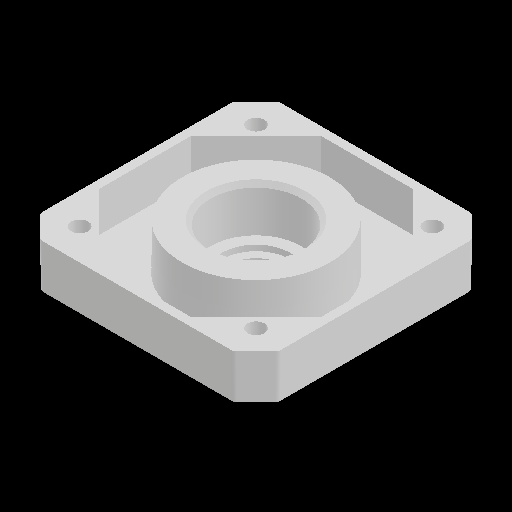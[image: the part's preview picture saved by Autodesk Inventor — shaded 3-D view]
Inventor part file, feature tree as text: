
AUTODESK INVENTOR PART (.ipt)
format: ipt  version: 2023 (Build 270158000, 158)  size: 175,616 bytes
history: native  units: mm
features: fillet x1
ambient origin geometry x8: Origin, YZ Plane, XZ Plane, XY Plane, X Axis, Y Axis, Z Axis, Center Point
bodies: Solid1 (feature_tree)
feature tree (1):
  fillet  "Fillet4"  [1 undecoded]
note: 1 required parameter value undecoded (feature->parameter linkage not recoverable at this tier; creation-order binding heuristic only, values carry confidence <= 0.55)
